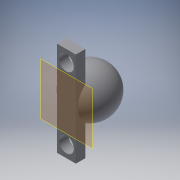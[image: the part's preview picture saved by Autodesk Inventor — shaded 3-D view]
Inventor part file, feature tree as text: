
AUTODESK INVENTOR PART (.ipt)
format: ipt  version: 2019 (Build 230136000, 136)  size: 135,680 bytes
history: native  units: mm
features: sketch x3, other x1, revolve x1, plane x1, extrude x1, hole x1
ambient origin geometry x8: Origin, YZ Plane, XZ Plane, XY Plane, X Axis, Y Axis, Z Axis, Center Point
bodies: Body1 (feature_tree)
feature tree (8):
  other  "Sólido1"
  revolve  "Revolución1"  [1 undecoded]
  plane  "Plano de trabajo1"
  extrude  "Extrusión1"  Depth=20.0mm
  hole  "Agujero1"  [1 undecoded]
  sketch  "Boceto1"  dims[d1=90.0deg d2=5.0mm]
  sketch  "Boceto2"  dims[d3=4.0mm d4=20.0mm]
  sketch  "Boceto3"  dims[d5=2.0mm d6=0.0mm d7=3.175mm d8=6.0mm d9=4.0mm d10=2.0mm d11=90.0deg d12=8.0mm d13=20.594885mm]
note: 2 required parameter values undecoded (feature->parameter linkage not recoverable at this tier; creation-order binding heuristic only, values carry confidence <= 0.55)